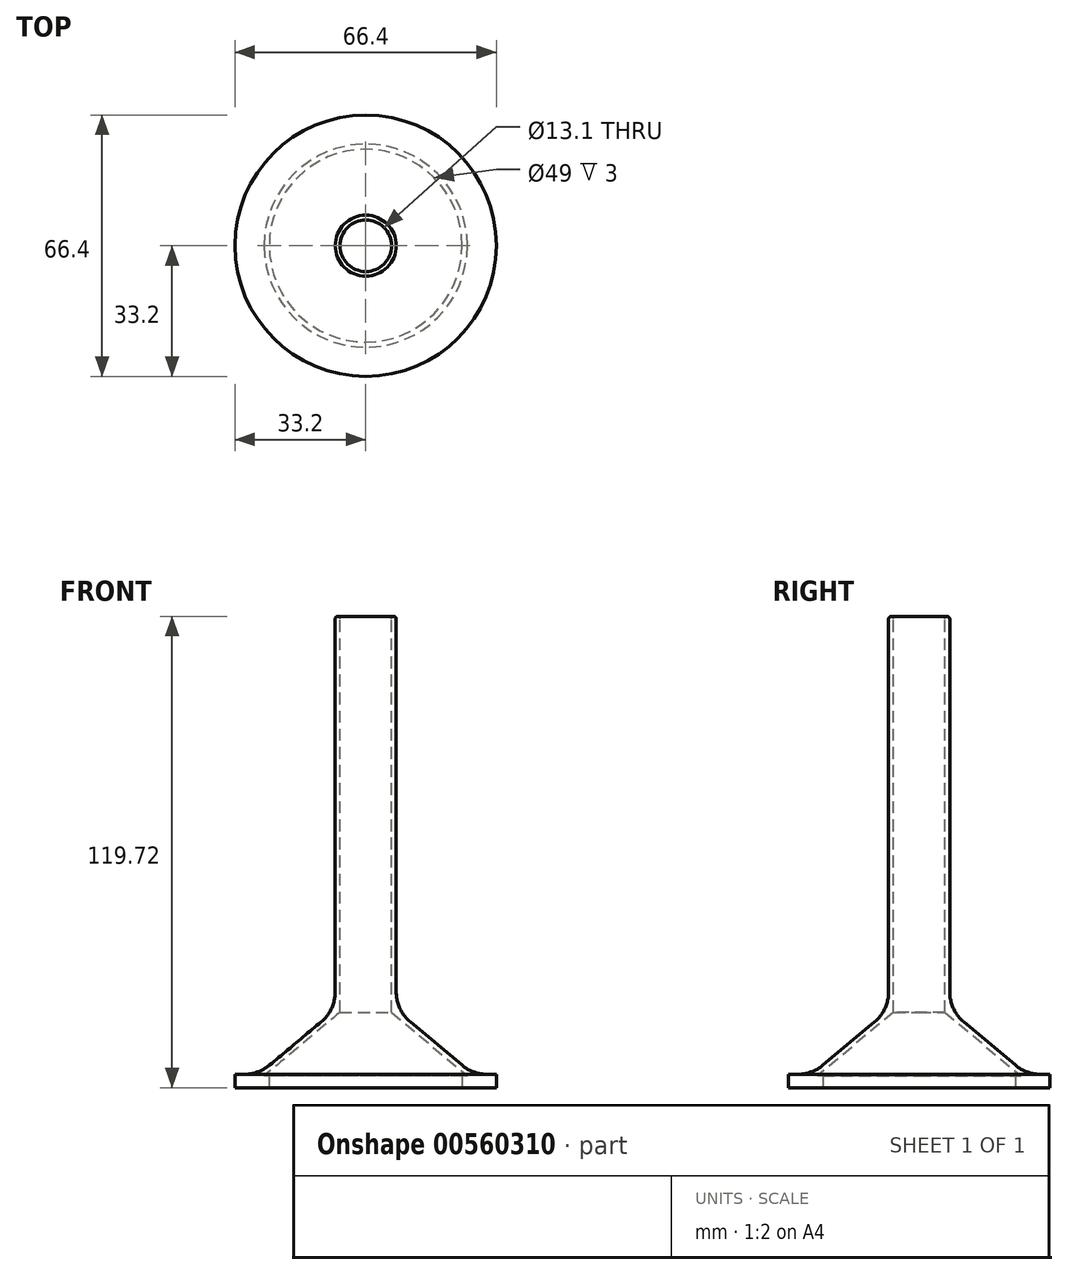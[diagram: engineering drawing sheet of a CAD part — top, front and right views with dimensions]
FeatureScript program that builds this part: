
annotation { "Feature Type Name" : "Feature", "Feature Type Description" : "" }
export const myFeature = defineFeature(function(context is Context, id is Id, definition is map)
    precondition{}
    {
        {
            var Q0;
            Q0=qCreatedBy(makeId("Front.planeOp"),FACE);
            var sketch = newSketch(context, id + "F0", { "sketchPlane" : qUnion([Q0])});
            skLineSegment(sketch, "E0", {"start": v(0, 0) * mm, "end": v(-33.2, 0) * mm});
            skLineSegment(sketch, "E1", {"start": v(-33.2, 0) * mm, "end": v(-33.2, 3.4) * mm});
            skLineSegment(sketch, "E2", {"start": v(-33.2, 3.4) * mm, "end": v(-27.2, 3.4) * mm});
            skLineSegment(sketch, "E3", {"start": v(-7.75, 119.72) * mm, "end": v(0, 119.72) * mm});
            skLineSegment(sketch, "E4", {"start": v(-7.75, 119.72) * mm, "end": v(-7.75, 19.72) * mm});
            skLineSegment(sketch, "E5", {"start": v(0, 119.72) * mm, "end": v(0, 0) * mm});
            skLineSegment(sketch, "E6", {"start": v(-27.2, 3.4) * mm, "end": v(-7.75, 19.72) * mm});
            skSolve(sketch);
        }
        {
            var Q0;
            Q0 = qSketchRegion(id + "F0", true);
            var Q1;
            Q1=sQuery(id+"F0.wireOp",EDGE,"E5");
            revolve(context, id + "F1", {"entities" : qUnion([Q0]), "axis" : qUnion([Q1]), "revolveType" : RevolveType.FULL});
        }
        {
            var Q0;
            Q0=makeQuery(id+"F1.opRevolve","SWEPT_FACE",FACE,{"disambiguationData":[OSD([sQuery(id+"F0.wireOp",EDGE,"E0")])]});
            var Q1;
            Q1=makeQuery(id+"F1.opRevolve","SWEPT_FACE",FACE,{"disambiguationData":[OSD([sQuery(id+"F0.wireOp",EDGE,"E3")])]});
            shell(context, id + "F2", {"entities" : qUnion([Q0, Q1]), "thickness" : 1.2 * mm});
        }
        {
            var Q0;
            Q0=qCreatedBy(makeId("Top.planeOp"),FACE);
            var sketch = newSketch(context, id + "F3", { "sketchPlane" : qUnion([Q0])});
            skCircle(sketch, "E7", {"center": v(0, 0) * mm, "radius": 33.2 * mm});
            skCircle(sketch, "E8", {"center": v(0, 0) * mm, "radius": 24.5 * mm});
            skSolve(sketch);
        }
        {
            var Q0;
            Q0=makeQuery(id+"F3.imprint","IMPRINT",FACE,{"disambiguationData":[TD([[makeQuery(id+"F3.imprint","IMPRINT",EDGE,{"derivedFrom":sQuery(id+"F3.wireOp",EDGE,"E7")}),1.0]])]});
            extrude(context, id + "F4", {"entities" : qUnion([Q0]), "operationType" : NewBodyOperationType.ADD, "depth" : 3 * mm, "offsetDistance" : 25 * mm});
        }
        {
            var Q0;
            Q0=makeQuery(id+"F2.opShell","OFFSET_EDGE",EDGE,{"disambiguationData":[OSD([sQuery(id+"F0.wireOp",EDGE,"E3"),sQuery(id+"F0.wireOp",EDGE,"E4")])]});
            var Q1;
            Q1=makeQuery(id+"F1.opRevolve","SWEPT_EDGE",EDGE,{"disambiguationData":[OSD([sQuery(id+"F0.wireOp",EDGE,"E3"),sQuery(id+"F0.wireOp",EDGE,"E4")])]});
            fillet(context, id + "F5", {"entities" : qUnion([Q0, Q1]), "radius" : 0.6 * mm, "tangentPropagation" : true, "allowEdgeOverflow" : false});
        }
        {
            var Q0;
            Q0=makeQuery(id+"F1.opRevolve","SWEPT_FACE",FACE,{"disambiguationData":[OSD([sQuery(id+"F0.wireOp",EDGE,"E6")])]});
            fillet(context, id + "F6", {"entities" : qUnion([Q0]), "radius" : 10 * mm, "tangentPropagation" : true, "allowEdgeOverflow" : false});
        }
    });
